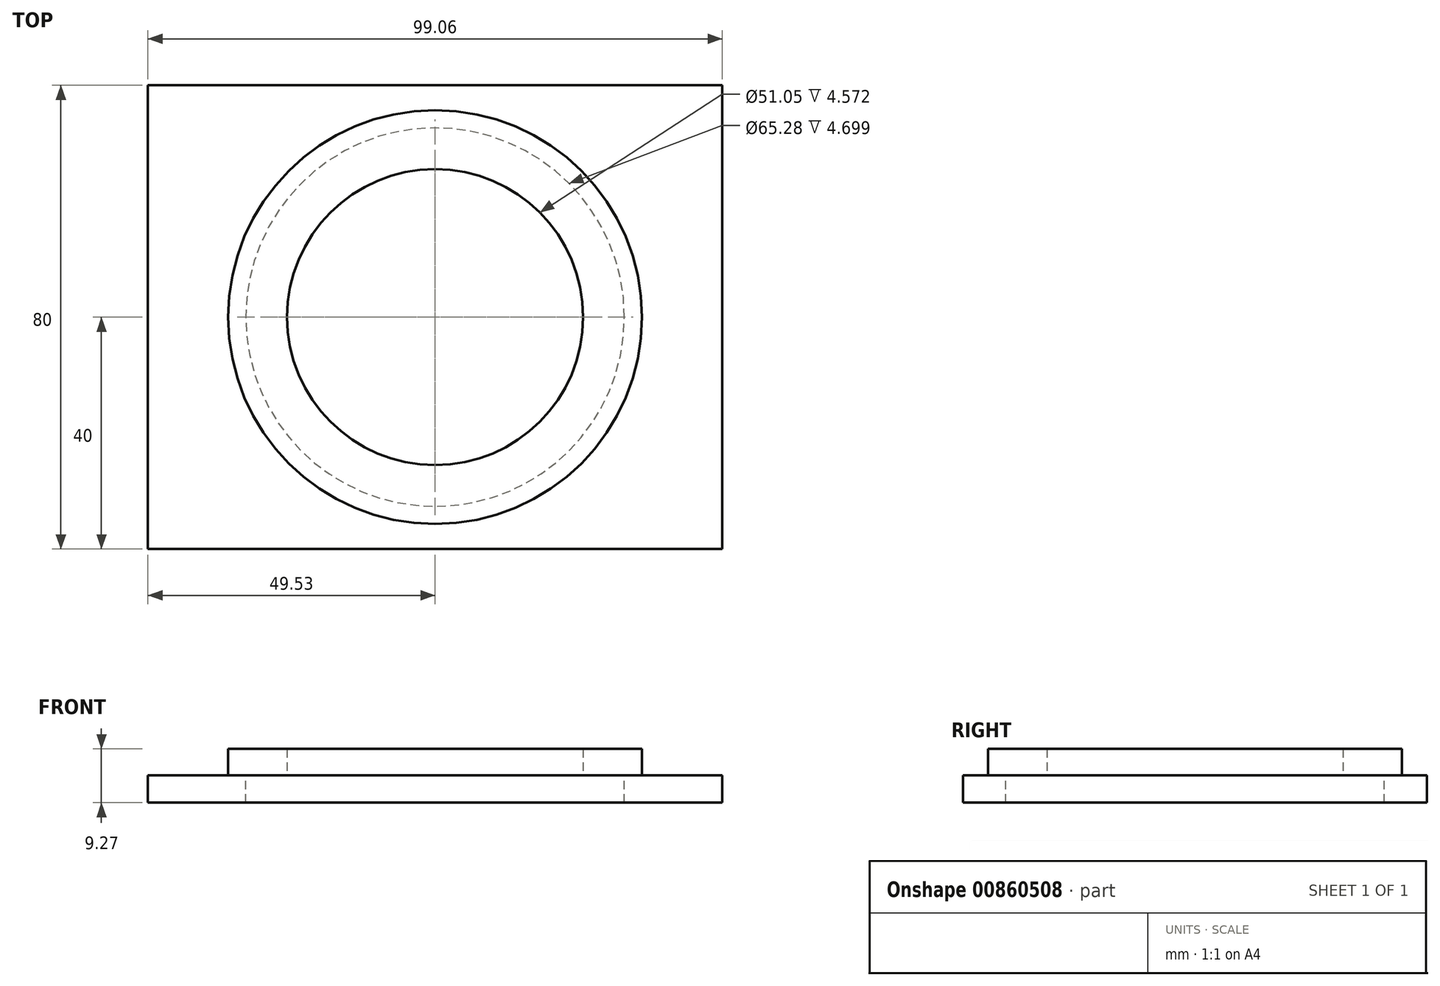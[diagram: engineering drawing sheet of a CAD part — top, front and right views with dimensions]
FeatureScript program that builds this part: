
annotation { "Feature Type Name" : "Feature", "Feature Type Description" : "" }
export const myFeature = defineFeature(function(context is Context, id is Id, definition is map)
    precondition{}
    {
        {
            var Q0;
            Q0=qCreatedBy(makeId("Top.planeOp"),FACE);
            var sketch = newSketch(context, id + "F0", { "sketchPlane" : qUnion([Q0])});
            skLineSegment(sketch, "E0.bottom", {"start": v(49.53, 40) * mm, "end": v(-49.53, 40) * mm});
            skLineSegment(sketch, "E0.top", {"start": v(49.53, -40) * mm, "end": v(-49.53, -40) * mm});
            skLineSegment(sketch, "E0.left", {"start": v(49.53, 40) * mm, "end": v(49.53, -40) * mm});
            skLineSegment(sketch, "E0.right", {"start": v(-49.53, 40) * mm, "end": v(-49.53, -40) * mm});
            skPoint(sketch, "E0.middle", {"position": v(0, 0) * mm});
            skCircle(sketch, "E1", {"center": v(0, 0) * mm, "radius": 4.76 * mm});
            skCircle(sketch, "E2", {"center": v(0, 0) * mm, "radius": 35.69 * mm});
            skCircle(sketch, "E3", {"center": v(0, 0) * mm, "radius": 25.53 * mm});
            skCircle(sketch, "E4", {"center": v(0, 0) * mm, "radius": 32.64 * mm});
            skSolve(sketch);
        }
        {
            var Q0;
            Q0=makeQuery(id+"F0.imprint","IMPRINT",FACE,{"disambiguationData":[TD([[makeQuery(id+"F0.imprint","IMPRINT",EDGE,{"derivedFrom":sQuery(id+"F0.wireOp",EDGE,"E0.bottom")}),1.0]])]});
            var Q1;
            Q1=makeQuery(id+"F0.imprint","IMPRINT",FACE,{"disambiguationData":[TD([[makeQuery(id+"F0.imprint","IMPRINT",EDGE,{"derivedFrom":sQuery(id+"F0.wireOp",EDGE,"E2")}),1.0]])]});
            extrude(context, id + "F1", {"entities" : qUnion([Q0, Q1]), "depth" : -4.7 * mm, "offsetDistance" : 25.4 * mm});
        }
        {
            var Q0;
            Q0=makeQuery(id+"F0.imprint","IMPRINT",FACE,{"disambiguationData":[TD([[makeQuery(id+"F0.imprint","IMPRINT",EDGE,{"derivedFrom":sQuery(id+"F0.wireOp",EDGE,"E2")}),1.0]])]});
            var Q1;
            Q1=makeQuery(id+"F0.imprint","IMPRINT",FACE,{"disambiguationData":[TD([[makeQuery(id+"F0.imprint","IMPRINT",EDGE,{"derivedFrom":sQuery(id+"F0.wireOp",EDGE,"E3")}),-1.0]])]});
            extrude(context, id + "F2", {"entities" : qUnion([Q0, Q1]), "depth" : 4.57 * mm, "offsetDistance" : 25.4 * mm});
        }
    });
